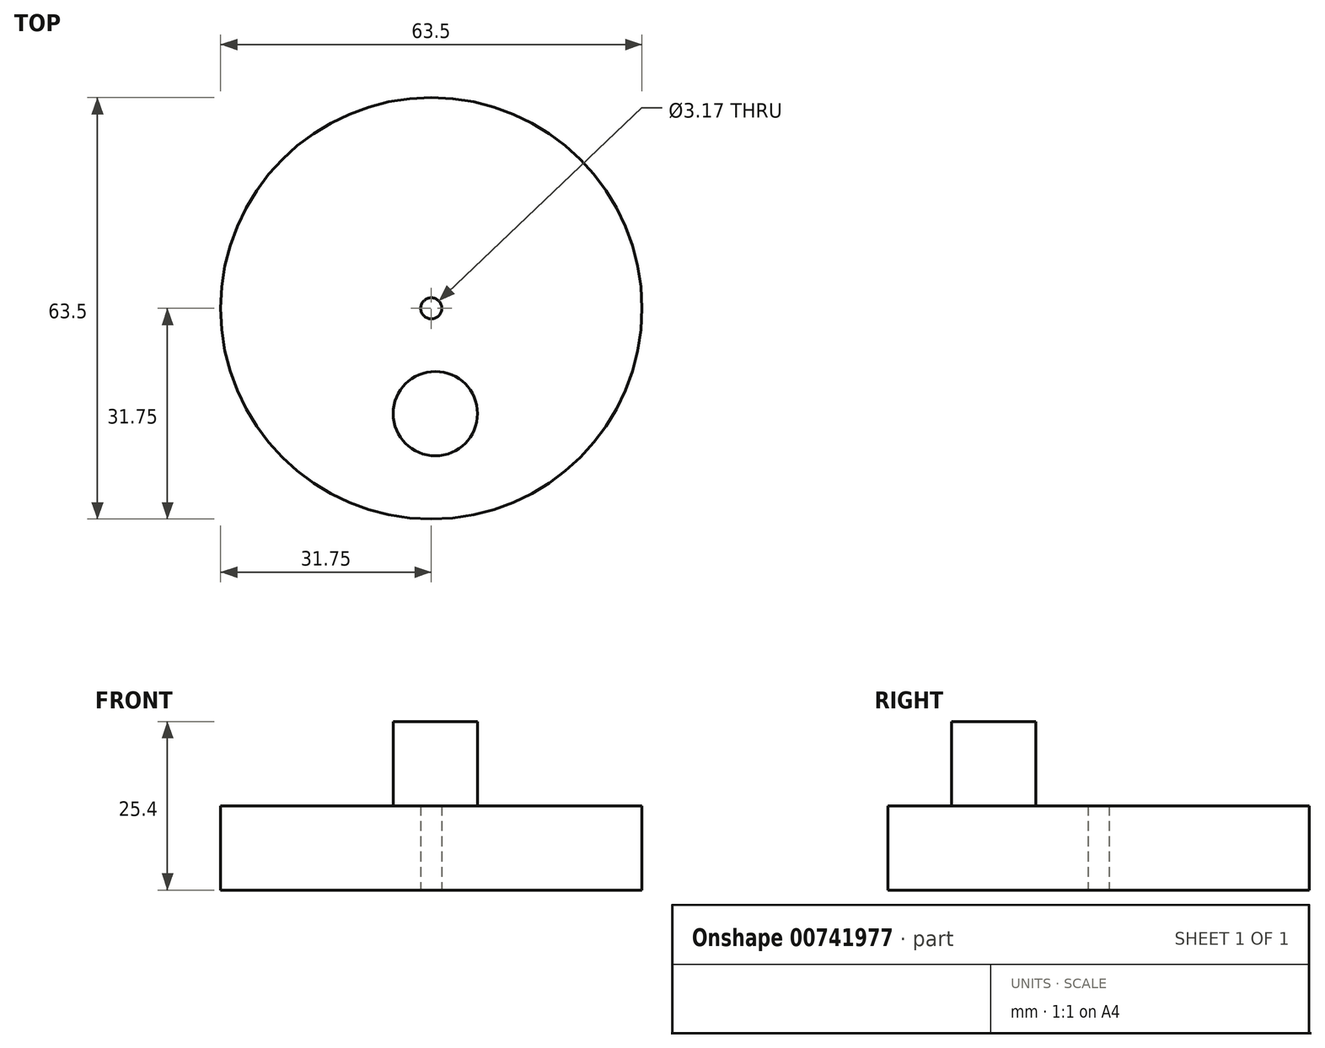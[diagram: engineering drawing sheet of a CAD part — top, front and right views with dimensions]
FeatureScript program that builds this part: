
annotation { "Feature Type Name" : "Feature", "Feature Type Description" : "" }
export const myFeature = defineFeature(function(context is Context, id is Id, definition is map)
    precondition{}
    {
        {
            var Q0;
            Q0=qCreatedBy(makeId("Top.planeOp"),FACE);
            var sketch = newSketch(context, id + "F0", { "sketchPlane" : qUnion([Q0])});
            skCircle(sketch, "E0", {"center": v(0, 0) * mm, "radius": 31.75 * mm});
            skCircle(sketch, "E1", {"center": v(0, 0) * mm, "radius": 1.59 * mm});
            skLineSegment(sketch, "E2", {"start": v(0, 0) * mm, "end": v(1.23, -31.73) * mm});
            skCircle(sketch, "E3", {"center": v(0.61, -15.86) * mm, "radius": 6.35 * mm});
            skSolve(sketch);
        }
        {
            var Q0;
            Q0 = qSketchRegion(id + "F0", true);
            extrude(context, id + "F1", {"entities" : qUnion([Q0]), "depth" : 12.7 * mm, "offsetDistance" : 25.4 * mm});
        }
        {
            var Q0;
            {var subQ0=sQuery(id+"F0.wireOp",EDGE,"E3");var subQ1=sQuery(id+"F0.wireOp",EDGE,"E2");var subQ2=makeQuery(id+"F0.imprint","INTERSECT",VERTEX,{"disambiguationData":[OD(0.0)],"derivedFrom":[subQ1,subQ0]});Q0=makeQuery(id+"F0.imprint","IMPRINT",FACE,{"disambiguationData":[TD([[makeQuery(id+"F0.imprint","IMPRINT",EDGE,{"disambiguationData":[TD([[subQ2,1.0]])],"derivedFrom":subQ1}),1.0]])]});}
            var Q1;
            {var subQ0=sQuery(id+"F0.wireOp",EDGE,"E3");var subQ1=sQuery(id+"F0.wireOp",EDGE,"E2");var subQ2=makeQuery(id+"F0.imprint","INTERSECT",VERTEX,{"disambiguationData":[OD(0.0)],"derivedFrom":[subQ1,subQ0]});Q1=makeQuery(id+"F0.imprint","IMPRINT",FACE,{"disambiguationData":[TD([[makeQuery(id+"F0.imprint","IMPRINT",EDGE,{"disambiguationData":[TD([[subQ2,1.0]])],"derivedFrom":subQ1}),-1.0]])]});}
            extrude(context, id + "F2", {"entities" : qUnion([Q0, Q1]), "operationType" : NewBodyOperationType.ADD, "depth" : 25.4 * mm, "offsetDistance" : 25.4 * mm});
        }
    });
